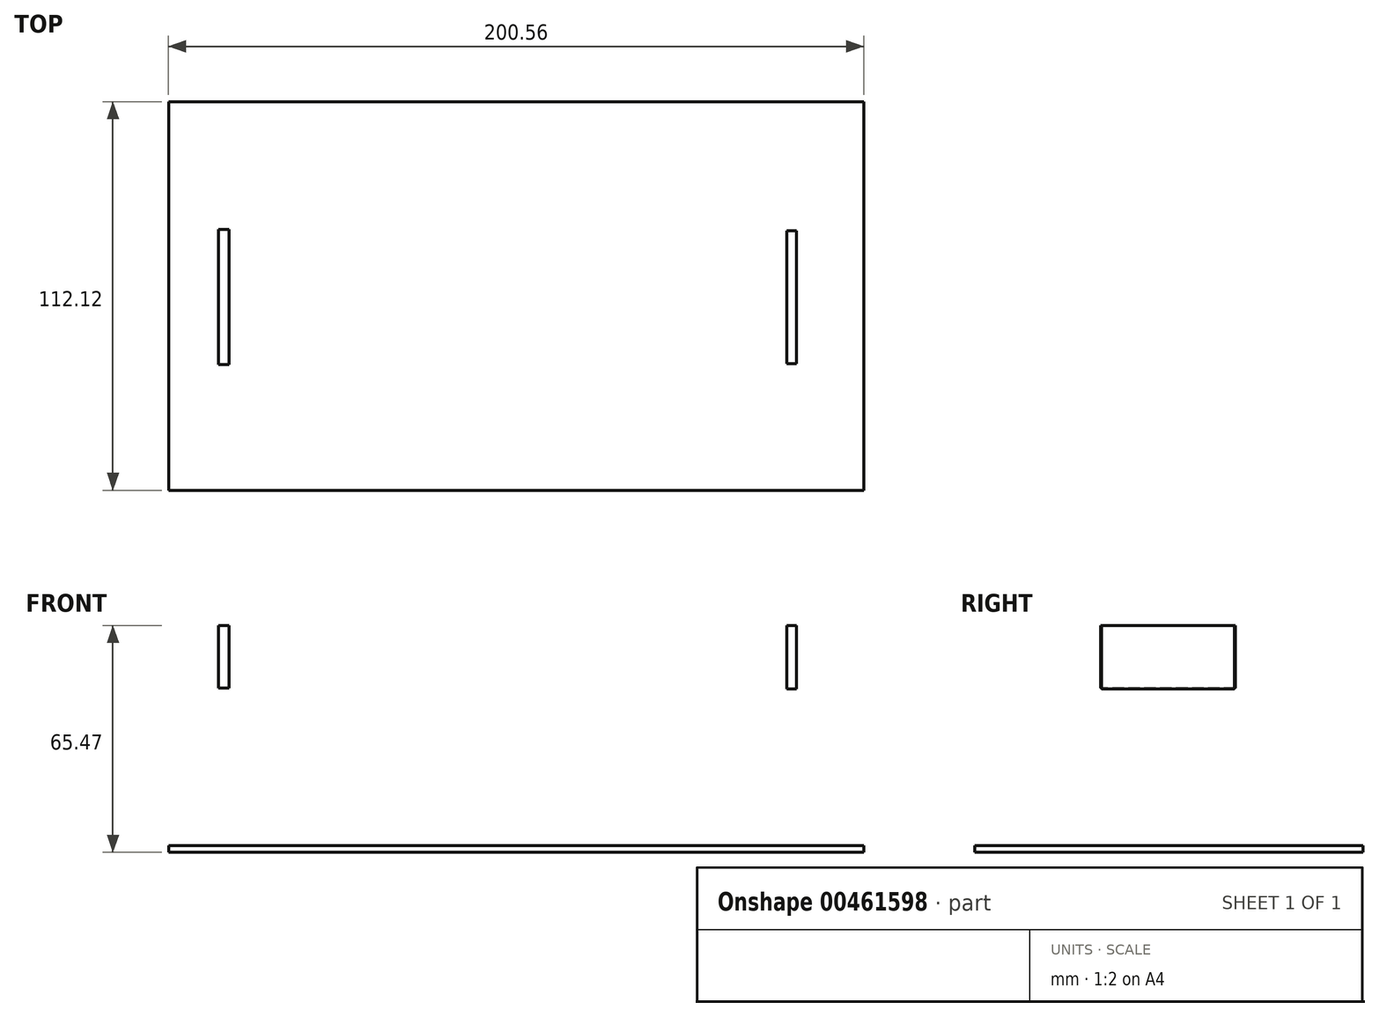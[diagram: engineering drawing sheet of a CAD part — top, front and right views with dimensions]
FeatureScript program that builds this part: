
annotation { "Feature Type Name" : "Feature", "Feature Type Description" : "" }
export const myFeature = defineFeature(function(context is Context, id is Id, definition is map)
    precondition{}
    {
        {
            var Q0;
            Q0=qCreatedBy(makeId("Top.planeOp"),FACE);
            var sketch = newSketch(context, id + "F0", { "sketchPlane" : qUnion([Q0])});
            skLineSegment(sketch, "E0.bottom", {"start": v(-100.28, 56.32) * mm, "end": v(100.28, 56.32) * mm});
            skLineSegment(sketch, "E0.top", {"start": v(-100.28, -55.8) * mm, "end": v(100.28, -55.8) * mm});
            skLineSegment(sketch, "E0.left", {"start": v(-100.28, 56.32) * mm, "end": v(-100.28, -55.8) * mm});
            skLineSegment(sketch, "E0.right", {"start": v(100.28, 56.32) * mm, "end": v(100.28, -55.8) * mm});
            skSolve(sketch);
        }
        {
            var Q0;
            Q0=qSketchRegion(id+"F0",true);
            extrude(context, id + "F1", {"entities" : qUnion([Q0]), "depth" : 1.95 * mm});
        }
        {
            var Q0;
            Q0=makeQuery(id+"F1.opExtrude","CAP_FACE",FACE,{"disambiguationData":[OSD([sQuery(id+"F0.wireOp",EDGE,"E0.bottom"),sQuery(id+"F0.wireOp",EDGE,"E0.top"),sQuery(id+"F0.wireOp",EDGE,"E0.left"),sQuery(id+"F0.wireOp",EDGE,"E0.right")])],"isStart":false});
            var sketch = newSketch(context, id + "F2", { "sketchPlane" : qUnion([Q0])});
            skCircle(sketch, "E1", {"center": v(-90.01, 0) * mm, "radius": 4.25 * mm});
            skCircle(sketch, "E2", {"center": v(83.96, -0.53) * mm, "radius": 4.25 * mm});
            skSolve(sketch);
        }
        {
            var Q0;
            Q0=sQuery(id+"F2.wireOp",EDGE,"E2");
            var Q1;
            Q1=sQuery(id+"F2.wireOp",EDGE,"E1");
            extrude(context, id + "F3", {"bodyType" : ToolBodyType.SURFACE, "surfaceEntities" : qUnion([Q0, Q1]), "depth" : 67.58 * mm});
        }
        {
            var Q0;
            Q0=makeQuery(id+"F1.opExtrude","CAP_FACE",FACE,{"disambiguationData":[OSD([sQuery(id+"F0.wireOp",EDGE,"E0.bottom"),sQuery(id+"F0.wireOp",EDGE,"E0.top"),sQuery(id+"F0.wireOp",EDGE,"E0.left"),sQuery(id+"F0.wireOp",EDGE,"E0.right")])],"isStart":false});
            var sketch = newSketch(context, id + "F4", { "sketchPlane" : qUnion([Q0])});
            skSolve(sketch);
        }
        {
            var Q0;
            Q0=qCreatedBy(makeId("Right.planeOp"),FACE);
            var sketch = newSketch(context, id + "F5", { "sketchPlane" : qUnion([Q0])});
            skLineSegment(sketch, "E3.bottom", {"start": v(19.14, 65.47) * mm, "end": v(-19.24, 65.47) * mm});
            skLineSegment(sketch, "E3.top", {"start": v(19.14, 47.12) * mm, "end": v(-19.24, 47.12) * mm});
            skLineSegment(sketch, "E3.left", {"start": v(19.14, 65.47) * mm, "end": v(19.14, 47.12) * mm});
            skLineSegment(sketch, "E3.right", {"start": v(-19.24, 65.47) * mm, "end": v(-19.24, 47.12) * mm});
            skSolve(sketch);
        }
        {
            var Q0;
            Q0=qSketchRegion(id+"F5",true);
            extrude(context, id + "F6", {"entities" : qUnion([Q0]), "depth" : 80.87 * mm, "hasSecondDirection" : true, "secondDirectionOppositeDirection" : false, "secondDirectionDepth" : 78.04 * mm});
        }
        {
            var Q0;
            Q0=qCreatedBy(makeId("Right.planeOp"),FACE);
            var sketch = newSketch(context, id + "F7", { "sketchPlane" : qUnion([Q0])});
            skLineSegment(sketch, "E4.bottom", {"start": v(19.46, 65.47) * mm, "end": v(-19.47, 65.47) * mm});
            skLineSegment(sketch, "E4.top", {"start": v(19.46, 47.4) * mm, "end": v(-19.47, 47.4) * mm});
            skLineSegment(sketch, "E4.left", {"start": v(19.46, 65.47) * mm, "end": v(19.46, 47.4) * mm});
            skLineSegment(sketch, "E4.right", {"start": v(-19.47, 65.47) * mm, "end": v(-19.47, 47.4) * mm});
            skSolve(sketch);
        }
        {
            var Q0;
            Q0=qSketchRegion(id+"F7",true);
            extrude(context, id + "F8", {"entities" : qUnion([Q0]), "oppositeDirection" : true, "depth" : 85.92 * mm, "hasSecondDirection" : true, "secondDirectionOppositeDirection" : true, "secondDirectionDepth" : 82.8 * mm});
        }
        {
            var Q0;
            Q0=qCreatedBy(makeId("Top.planeOp"),FACE);
            var sketch = newSketch(context, id + "F9", { "sketchPlane" : qUnion([Q0])});
            skCircle(sketch, "E5", {"center": v(-75.77, 0) * mm, "radius": 7.5 * mm});
            skCircle(sketch, "E6", {"center": v(68.94, 0.34) * mm, "radius": 7.85 * mm});
            skSolve(sketch);
        }
        {
            var Q0;
            Q0=sQuery(id+"F9.wireOp",EDGE,"E5");
            extrude(context, id + "F10", {"bodyType" : ToolBodyType.SURFACE, "surfaceEntities" : qUnion([Q0]), "depth" : 54.58 * mm, "hasSecondDirection" : true, "secondDirectionOppositeDirection" : false, "secondDirectionDepth" : 50.25 * mm});
        }
        {
            var Q0;
            Q0=sQuery(id+"F9.wireOp",EDGE,"E6");
            extrude(context, id + "F11", {"bodyType" : ToolBodyType.SURFACE, "surfaceEntities" : qUnion([Q0]), "depth" : 55.1 * mm, "hasSecondDirection" : true, "secondDirectionOppositeDirection" : false, "secondDirectionDepth" : 50.88 * mm});
        }
    });
